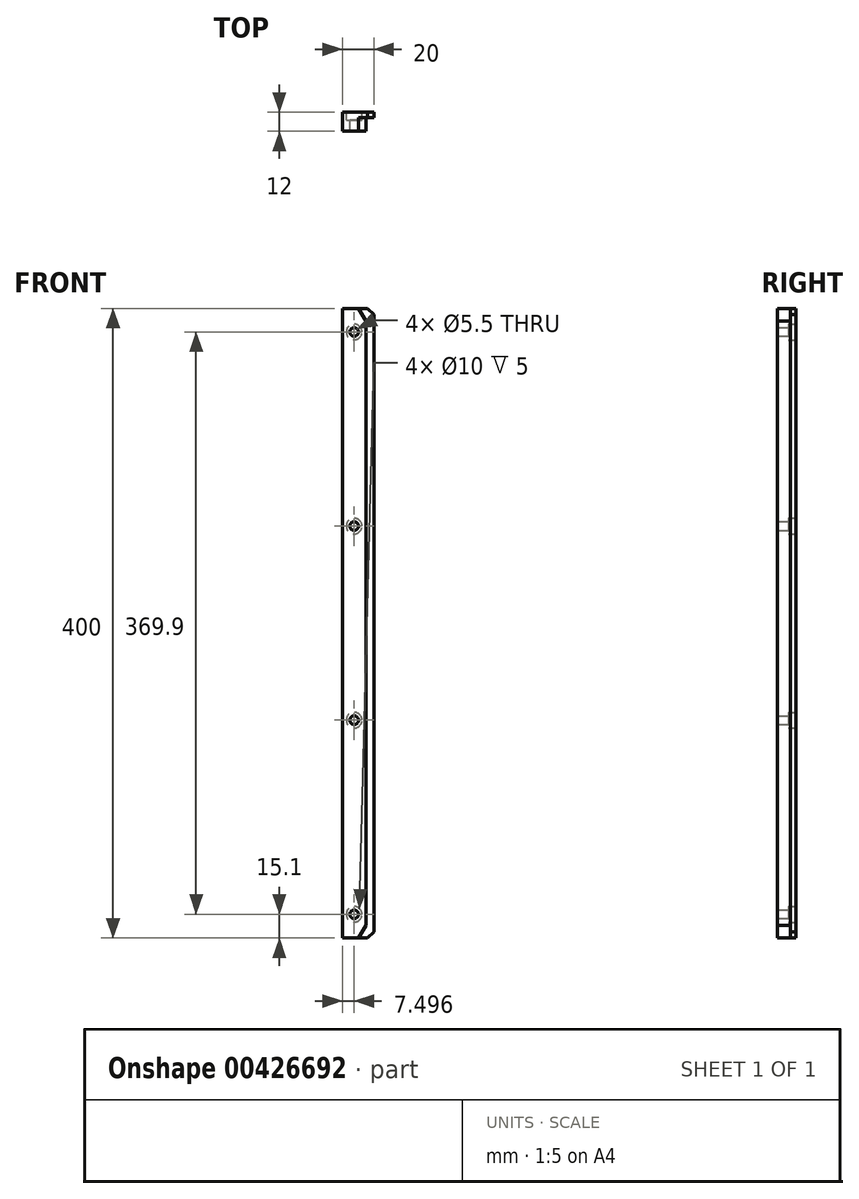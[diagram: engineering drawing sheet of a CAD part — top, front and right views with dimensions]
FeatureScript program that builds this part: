
annotation { "Feature Type Name" : "Feature", "Feature Type Description" : "" }
export const myFeature = defineFeature(function(context is Context, id is Id, definition is map)
    precondition{}
    {
        {
            var Q0;
            Q0=qCreatedBy(makeId("Top.planeOp"),FACE);
            var sketch = newSketch(context, id + "F0", { "sketchPlane" : qUnion([Q0])});
            skLineSegment(sketch, "E0.bottom", {"start": v(-15.78, -6.27) * mm, "end": v(4.22, -6.27) * mm});
            skLineSegment(sketch, "E0.top", {"start": v(-15.78, -18.27) * mm, "end": v(-0.78, -18.27) * mm});
            skLineSegment(sketch, "E0.left", {"start": v(-15.78, -6.27) * mm, "end": v(-15.78, -18.27) * mm});
            skLineSegment(sketch, "E0.right", {"start": v(4.22, -6.27) * mm, "end": v(4.22, -9.77) * mm});
            skLineSegment(sketch, "E1.0", {"start": v(-0.78, -9.77) * mm, "end": v(-0.78, -18.27) * mm});
            skLineSegment(sketch, "E2.0", {"start": v(-0.78, -9.77) * mm, "end": v(4.22, -9.77) * mm});
            skSolve(sketch);
        }
        {
            var Q0;
            Q0=makeQuery(id+"F0.imprint","IMPRINT",FACE,{"disambiguationData":[TD([[makeQuery(id+"F0.imprint","IMPRINT",EDGE,{"derivedFrom":sQuery(id+"F0.wireOp",EDGE,"E0.bottom")}),-1.0]])]});
            extrude(context, id + "F1", {"entities" : qUnion([Q0]), "depth" : 400 * mm});
        }
        {
            var Q0;
            Q0=makeQuery(id+"F1.opExtrude","SWEPT_FACE",FACE,{"disambiguationData":[OSD([sQuery(id+"F0.wireOp",EDGE,"E0.bottom")])]});
            var sketch = newSketch(context, id + "F2", { "sketchPlane" : qUnion([Q0])});
            skLineSegment(sketch, "E3.0", {"start": v(8.28, 400) * mm, "end": v(8.28, 0) * mm});
            skLineSegment(sketch, "E4.0", {"start": v(15.78, 385) * mm, "end": v(-4.22, 385) * mm});
            skLineSegment(sketch, "E5.0", {"start": v(15.78, 261.7) * mm, "end": v(-4.22, 261.7) * mm});
            skLineSegment(sketch, "E6.0", {"start": v(15.78, 138.4) * mm, "end": v(-4.22, 138.4) * mm});
            skLineSegment(sketch, "E7.0", {"start": v(15.78, 15.1) * mm, "end": v(-4.22, 15.1) * mm});
            skLineSegment(sketch, "E8.bottom", {"start": v(15.78, 0) * mm, "end": v(-4.22, 0) * mm});
            skLineSegment(sketch, "E8.top", {"start": v(15.78, 400) * mm, "end": v(-4.22, 400) * mm});
            skLineSegment(sketch, "E8.left", {"start": v(15.78, 0) * mm, "end": v(15.78, 400) * mm});
            skLineSegment(sketch, "E8.right", {"start": v(-4.22, 0) * mm, "end": v(-4.22, 400) * mm});
            skPoint(sketch, "E9", {"position": v(8.28, 385) * mm});
            skPoint(sketch, "E10", {"position": v(8.28, 261.7) * mm});
            skPoint(sketch, "E11", {"position": v(8.28, 138.4) * mm});
            skPoint(sketch, "E12", {"position": v(8.28, 15.1) * mm});
            skSolve(sketch);
        }
        {
            var Q0;
            Q0=makeQuery(id+"F1.opExtrude","CAP_EDGE",EDGE,{"disambiguationData":[OSD([sQuery(id+"F0.wireOp",EDGE,"E0.right")])],"isStart":false});
            var Q1;
            Q1=makeQuery(id+"F1.opExtrude","CAP_EDGE",EDGE,{"disambiguationData":[OSD([sQuery(id+"F0.wireOp",EDGE,"E0.right")])],"isStart":true});
            chamfer(context, id + "F3", {"entities" : qUnion([Q0, Q1]), "width" : 4 * mm, "tangentPropagation" : true});
        }
        {
            var Q0;
            Q0=makeQuery(id+"F1.opExtrude","SWEPT_FACE",FACE,{"disambiguationData":[OSD([sQuery(id+"F0.wireOp",EDGE,"E0.top")])]});
            var sketch = newSketch(context, id + "F4", { "sketchPlane" : qUnion([Q0])});
            skLineSegment(sketch, "E13.right", {"start": v(-0.78, 400) * mm, "end": v(-0.78, 392) * mm});
            skLineSegment(sketch, "E14", {"start": v(-0.78, 8) * mm, "end": v(-5.4, 0) * mm});
            skLineSegment(sketch, "E15", {"start": v(-0.78, 392) * mm, "end": v(-5.4, 400) * mm});
            skLineSegment(sketch, "E16", {"start": v(-5.4, 400) * mm, "end": v(-0.78, 400) * mm});
            skLineSegment(sketch, "E17", {"start": v(-0.78, 8) * mm, "end": v(-0.78, 0) * mm});
            skLineSegment(sketch, "E18", {"start": v(-5.4, 0) * mm, "end": v(-0.78, 0) * mm});
            skSolve(sketch);
        }
        {
            var Q0;
            Q0=makeQuery(id+"F4.imprint","IMPRINT",FACE,{"disambiguationData":[TD([[makeQuery(id+"F4.imprint","IMPRINT",EDGE,{"derivedFrom":sQuery(id+"F4.wireOp",EDGE,"E13.right")}),-1.0]])]});
            var Q1;
            Q1=makeQuery(id+"F4.imprint","IMPRINT",FACE,{"disambiguationData":[TD([[makeQuery(id+"F4.imprint","IMPRINT",EDGE,{"derivedFrom":sQuery(id+"F4.wireOp",EDGE,"E14")}),1.0]])]});
            extrude(context, id + "F5", {"entities" : qUnion([Q0, Q1]), "operationType" : NewBodyOperationType.REMOVE, "oppositeDirection" : true, "depth" : 8.5 * mm});
        }
        {
            var Q0;
            Q0=sQuery(id+"F2.wireOp",VERTEX,"E12");
            var Q1;
            Q1=sQuery(id+"F2.wireOp",VERTEX,"E11");
            var Q2;
            Q2=sQuery(id+"F2.wireOp",VERTEX,"E10");
            var Q3;
            Q3=sQuery(id+"F2.wireOp",VERTEX,"E9");
            var Q4;
            Q4=makeQuery(id+"F1.opExtrude","SWEPT_BODY",BODY,{"disambiguationData":[OSD([sQuery(id+"F0.wireOp",EDGE,"E0.bottom"),sQuery(id+"F0.wireOp",EDGE,"E0.top"),sQuery(id+"F0.wireOp",EDGE,"E0.left"),sQuery(id+"F0.wireOp",EDGE,"E0.right"),sQuery(id+"F0.wireOp",EDGE,"E1.0"),sQuery(id+"F0.wireOp",EDGE,"E2.0")])]});
            hole(context, id + "F6", {"style" : HoleStyle.C_BORE, "endStyle" : HoleEndStyle.THROUGH, "holeDiameter" : 5.5 * mm, "cBoreDiameter" : 10 * mm, "cBoreDepth" : 5 * mm, "isTappedThrough" : true, "tappedDepth" : 10 * mm, "tapClearance" : 3, "locations" : qUnion([Q0, Q1, Q2, Q3]), "scope" : qUnion([Q4])});
        }
    });
